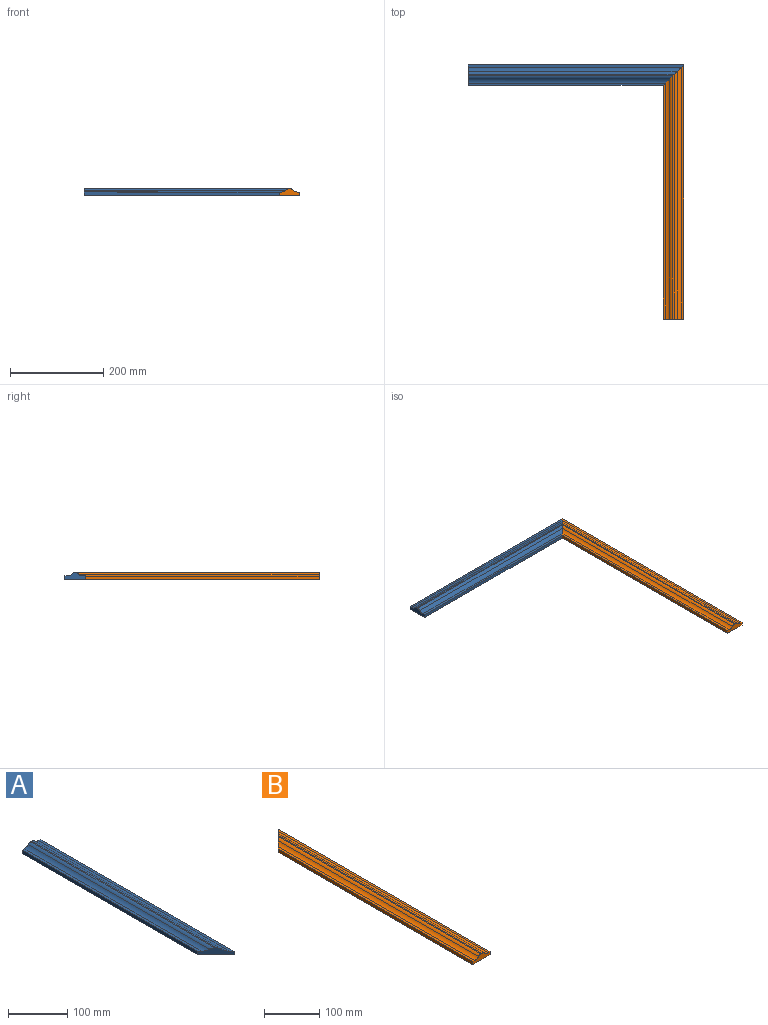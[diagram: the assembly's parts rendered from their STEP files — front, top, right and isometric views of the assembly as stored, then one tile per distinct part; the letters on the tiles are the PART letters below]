
ASSEMBLY  parts=2 mates=1
PART A: 12 faces, bbox 44x462x14 mm
  f0: cylinder r=9.73mm len=438.77mm, axis (0,1,0), area 3162.4mm2, adj f1,f9,f10,f11
  f1: cylinder r=12.89mm len=432.34mm, axis (0,1,0), area 4467.5mm2, adj f0,f2,f10,f11
  f2: plane 423x5mm, normal (0,0,1), area 2102.5mm2, adj f1,f3,f10,f11
  f3: plane 418x7mm, normal (-1,0,0), area 2926mm2, adj f2,f4,f10,f11
  f4: plane 462x44mm, normal (0,0,-1), area 19360mm2, adj f3,f5,f10,f11
  f5: plane 462x7mm, normal (1,0,0), area 3234mm2, adj f4,f6,f10,f11
  f6: plane 462x5mm, normal (0,0,1), area 2297.5mm2, adj f5,f7,f10,f11
  f7: cylinder r=12.89mm len=457mm, axis (0,1,0), area 4719.3mm2, adj f6,f8,f10,f11
  f8: cylinder r=9.73mm len=447.66mm, axis (0,1,0), area 3229.7mm2, adj f7,f9,f10,f11
  f9: plane 441.23x2.47mm, normal (0,0,1), area 1085mm2, adj f0,f8,f10,f11
  f10: plane 44x44mm, normal (-0.71,-0.71,0), area 601.7mm2, adj f0,f1,f2,f3,f4,f5,f6,f7
  f11: plane 44x14mm, normal (0,1,0), area 425.5mm2, adj f0,f1,f2,f3,f4,f5,f6,f7
PART B: 12 faces, bbox 44x545x14 mm
  f0: cylinder r=9.73mm len=521.77mm, axis (0,1,0), area 3765.3mm2, adj f1,f9,f10,f11
  f1: cylinder r=12.89mm len=515.34mm, axis (0,1,0), area 5334mm2, adj f0,f2,f10,f11
  f2: plane 506x5mm, normal (0,0,1), area 2517.5mm2, adj f1,f3,f10,f11
  f3: plane 501x7mm, normal (-1,0,0), area 3507mm2, adj f2,f4,f10,f11
  f4: plane 545x44mm, normal (0,0,-1), area 23012mm2, adj f3,f5,f10,f11
  f5: plane 545x7mm, normal (1,0,0), area 3815mm2, adj f4,f6,f10,f11
  f6: plane 545x5mm, normal (0,0,1), area 2712.5mm2, adj f5,f7,f10,f11
  f7: cylinder r=12.89mm len=540mm, axis (0,1,0), area 5585.8mm2, adj f6,f8,f10,f11
  f8: cylinder r=9.73mm len=530.66mm, axis (0,1,0), area 3832.6mm2, adj f7,f9,f10,f11
  f9: plane 524.23x2.47mm, normal (0,0,1), area 1289.7mm2, adj f0,f8,f10,f11
  f10: plane 44x14mm, normal (0,-1,0), area 425.5mm2, adj f0,f1,f2,f3,f4,f5,f6,f7
  f11: plane 44x44mm, normal (-0.71,0.71,0), area 601.7mm2, adj f0,f1,f2,f3,f4,f5,f6,f7
PLACE A rot(axis=(0,0,1),90deg) t=(-321.87,225.78,60.66)mm
PLACE B t=(-112.87,-24.72,60.66)mm
MATE fastened A.f10 <-> B.f11  axis (0.71,-0.71,0) through (-112.87,225.78,53.66)mm
